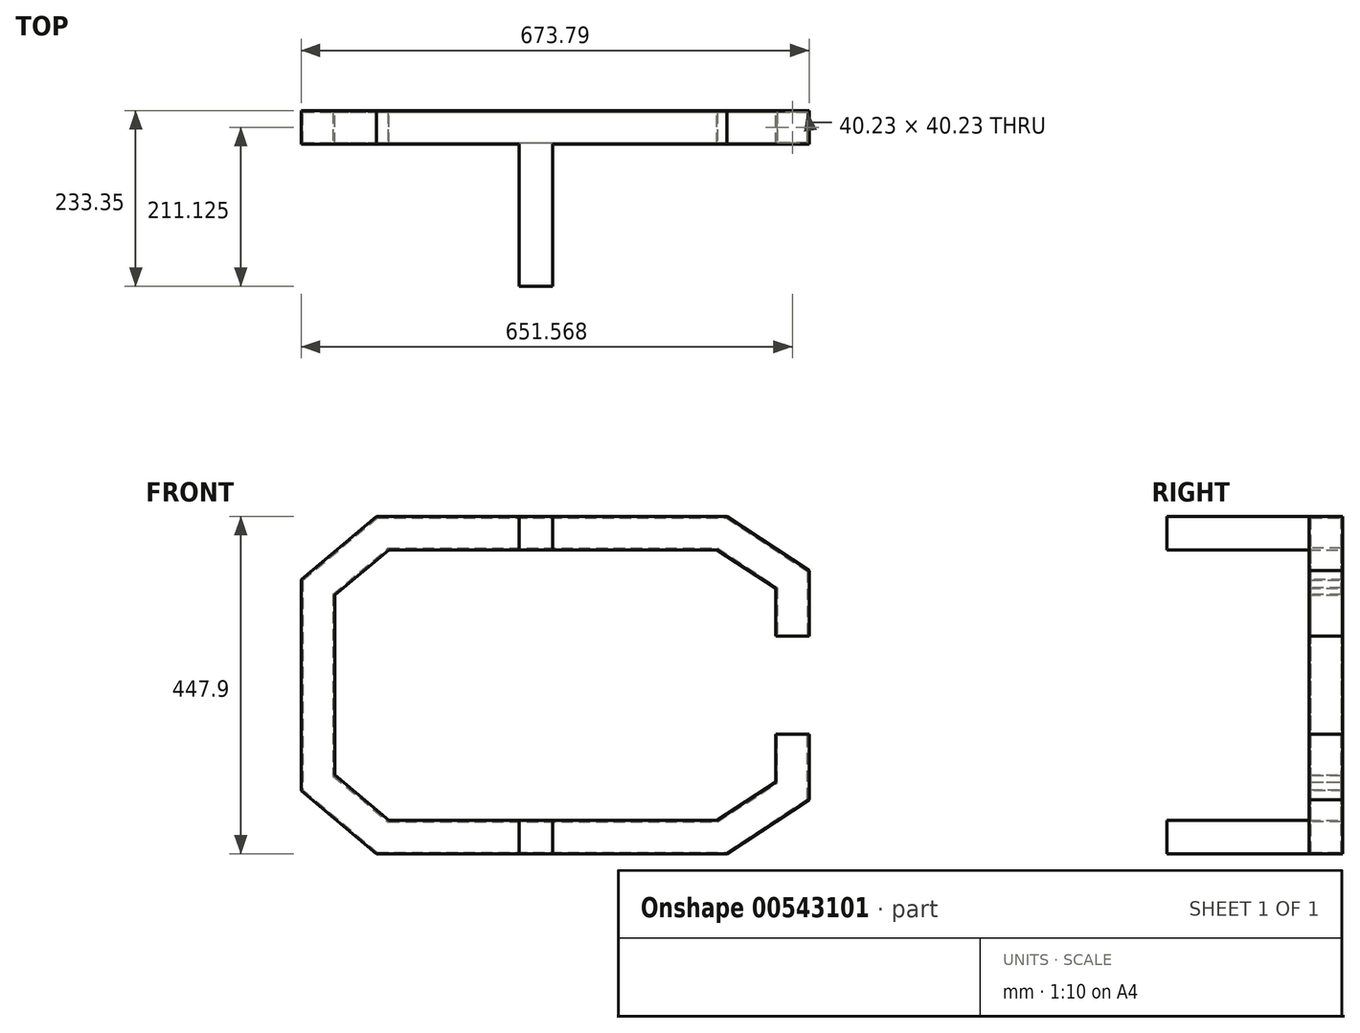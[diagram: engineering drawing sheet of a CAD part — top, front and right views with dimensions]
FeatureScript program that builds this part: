
annotation { "Feature Type Name" : "Feature", "Feature Type Description" : "" }
export const myFeature = defineFeature(function(context is Context, id is Id, definition is map)
    precondition{}
    {
        {
            var Q0;
            Q0=qCreatedBy(makeId("Top.planeOp"),FACE);
            var sketch = newSketch(context, id + "F0", { "sketchPlane" : qUnion([Q0])});
            skLineSegment(sketch, "E0.bottom", {"start": v(0, 0) * mm, "end": v(44.45, 0) * mm});
            skLineSegment(sketch, "E0.top", {"start": v(0, 44.45) * mm, "end": v(44.45, 44.45) * mm});
            skLineSegment(sketch, "E0.left", {"start": v(0, 0) * mm, "end": v(0, 44.45) * mm});
            skLineSegment(sketch, "E0.right", {"start": v(44.45, 0) * mm, "end": v(44.45, 44.45) * mm});
            skLineSegment(sketch, "E1.bottom", {"start": v(2.1, 2.1) * mm, "end": v(42.34, 2.1) * mm});
            skLineSegment(sketch, "E1.top", {"start": v(2.1, 42.34) * mm, "end": v(42.34, 42.34) * mm});
            skLineSegment(sketch, "E1.left", {"start": v(2.1, 2.1) * mm, "end": v(2.1, 42.34) * mm});
            skLineSegment(sketch, "E1.right", {"start": v(42.34, 2.1) * mm, "end": v(42.34, 42.34) * mm});
            skSolve(sketch);
        }
        {
            var Q0;
            Q0=qCreatedBy(makeId("Front.planeOp"),FACE);
            var sketch = newSketch(context, id + "F1", { "sketchPlane" : qUnion([Q0])});
            skLineSegment(sketch, "E2", {"start": v(-26.41, -152.4) * mm, "end": v(-26.41, 0) * mm});
            skLineSegment(sketch, "E3", {"start": v(-26.41, -152.4) * mm, "end": v(90.33, -250.36) * mm});
            skLineSegment(sketch, "E4", {"start": v(572.93, -250.36) * mm, "end": v(700.2, -166.53) * mm});
            skLineSegment(sketch, "E5", {"start": v(90.33, -250.36) * mm, "end": v(572.93, -250.36) * mm});
            skLineSegment(sketch, "E6", {"start": v(700.2, -166.53) * mm, "end": v(700.2, -64.93) * mm});
            skSolve(sketch);
        }
        {
            var Q0;
            Q0 = qSketchRegion(id + "F0", true);
            var Q1;
            Q1 = qConstructionFilter(qBodyType(qCreatedBy(id + "F1" ,EDGE), BodyType.WIRE), ConstructionObject.NO);
            sweep(context, id + "F2", {"profiles" : qUnion([Q0]), "path" : qUnion([Q1])});
        }
        {
            var Q0;
            Q0=makeQuery(id+"F2.opSweep","SWEPT_BODY",BODY,{"disambiguationData":[OSD([sQuery(id+"F0.wireOp",EDGE,"E0.bottom"),sQuery(id+"F0.wireOp",EDGE,"E0.top"),sQuery(id+"F0.wireOp",EDGE,"E0.left"),sQuery(id+"F0.wireOp",EDGE,"E0.right"),sQuery(id+"F0.wireOp",EDGE,"E1.bottom"),sQuery(id+"F0.wireOp",EDGE,"E1.top"),sQuery(id+"F0.wireOp",EDGE,"E1.left"),sQuery(id+"F0.wireOp",EDGE,"E1.right"),sQuery(id+"F1.wireOp",EDGE,"E6")])]});
            var Q1;
            Q1=qCreatedBy(makeId("Top.planeOp"),FACE);
            mirror(context, id + "F3", {"operationType" : NewBodyOperationType.ADD, "entities" : qUnion([Q0]), "mirrorPlane" : qUnion([Q1])});
        }
        {
            var Q0;
            {var subQ0=makeQuery(id+"F2.opSweep","SWEPT_FACE",FACE,{"disambiguationData":[OSD([sQuery(id+"F0.wireOp",EDGE,"E0.bottom"),sQuery(id+"F1.wireOp",EDGE,"E2")])]});Q0=makeQuery(id+"F3.boolean.opBoolean","MERGE",FACE,{"derivedFrom":[subQ0,makeQuery(id+"F3.opPattern","COPY",FACE,{"derivedFrom":subQ0,"instanceName":"1"})]});}
            var sketch = newSketch(context, id + "F4", { "sketchPlane" : qUnion([Q0])});
            skLineSegment(sketch, "E7.bottom", {"start": v(289.46, -223.95) * mm, "end": v(333.9, -223.95) * mm});
            skLineSegment(sketch, "E7.top", {"start": v(289.46, -179.5) * mm, "end": v(333.9, -179.5) * mm});
            skLineSegment(sketch, "E7.left", {"start": v(289.46, -223.95) * mm, "end": v(289.46, -179.5) * mm});
            skLineSegment(sketch, "E7.right", {"start": v(333.9, -223.95) * mm, "end": v(333.9, -179.5) * mm});
            skSolve(sketch);
        }
        {
            var Q0;
            Q0=makeQuery(id+"F2.opSweep","SWEPT_FACE",FACE,{"disambiguationData":[OSD([sQuery(id+"F0.wireOp",EDGE,"E0.left"),sQuery(id+"F1.wireOp",EDGE,"E5")])]});
            var sketch = newSketch(context, id + "F5", { "sketchPlane" : qUnion([Q0])});
            skLineSegment(sketch, "E8", {"start": v(310.84, 21.9) * mm, "end": v(310.84, 210.8) * mm});
            skSolve(sketch);
        }
        {
            var Q0;
            Q0=makeQuery(id+"F4.imprint","IMPRINT",FACE,{"disambiguationData":[TD([[makeQuery(id+"F4.imprint","IMPRINT",EDGE,{"derivedFrom":sQuery(id+"F4.wireOp",EDGE,"E7.bottom")}),1.0]])]});
            var Q1;
            Q1=sQuery(id+"F5.wireOp",EDGE,"E8");
            sweep(context, id + "F6", {"operationType" : NewBodyOperationType.ADD, "profiles" : qUnion([Q0]), "path" : qUnion([Q1])});
        }
        {
            var Q0;
            Q0=makeQuery(id+"F2.opSweep","SWEPT_BODY",BODY,{"disambiguationData":[OSD([sQuery(id+"F0.wireOp",EDGE,"E0.bottom"),sQuery(id+"F0.wireOp",EDGE,"E0.top"),sQuery(id+"F0.wireOp",EDGE,"E0.left"),sQuery(id+"F0.wireOp",EDGE,"E0.right"),sQuery(id+"F0.wireOp",EDGE,"E1.bottom"),sQuery(id+"F0.wireOp",EDGE,"E1.top"),sQuery(id+"F0.wireOp",EDGE,"E1.left"),sQuery(id+"F0.wireOp",EDGE,"E1.right"),sQuery(id+"F1.wireOp",EDGE,"E6")])]});
            var Q1;
            Q1=qCreatedBy(makeId("Top.planeOp"),FACE);
            mirror(context, id + "F7", {"operationType" : NewBodyOperationType.ADD, "entities" : qUnion([Q0]), "mirrorPlane" : qUnion([Q1])});
        }
    });
